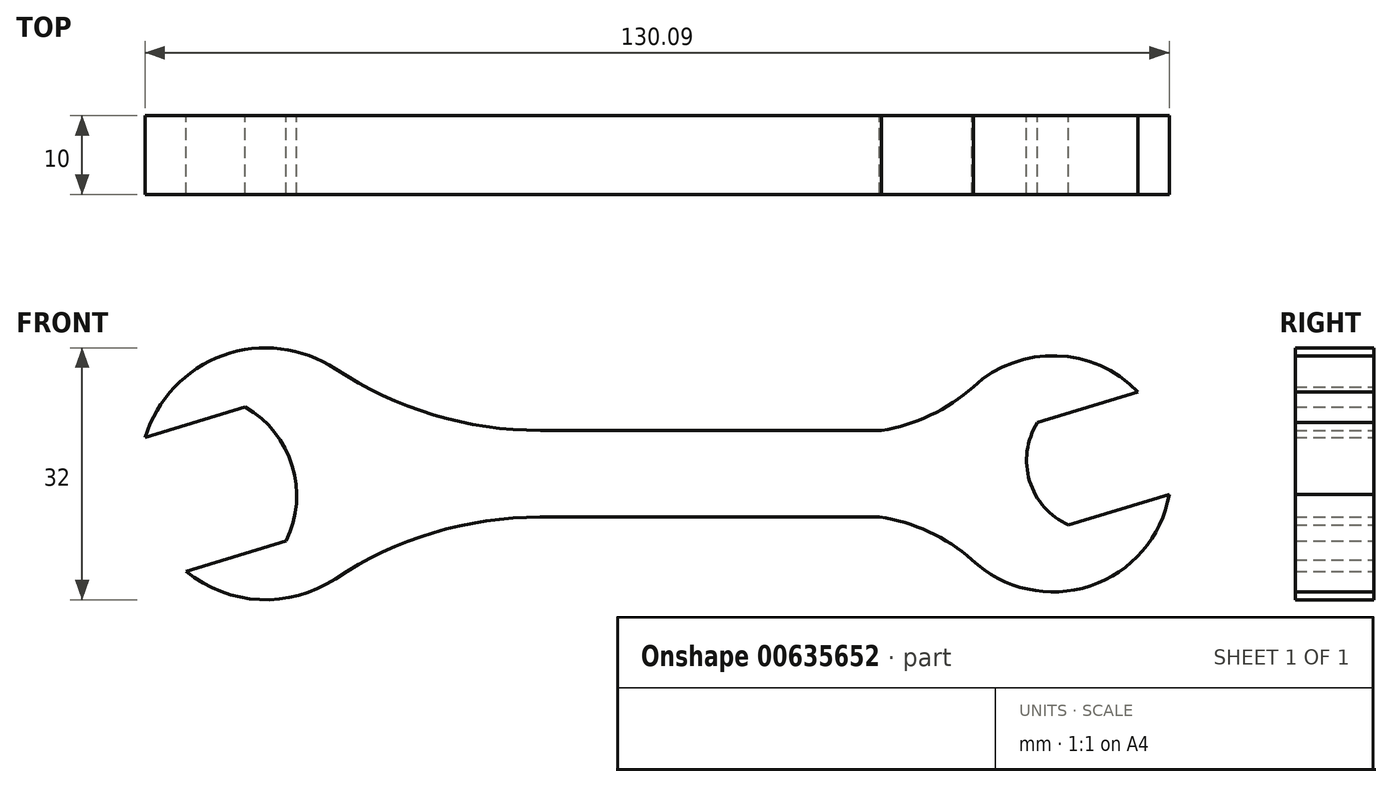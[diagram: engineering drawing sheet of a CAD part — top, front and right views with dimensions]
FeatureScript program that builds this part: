
annotation { "Feature Type Name" : "Feature", "Feature Type Description" : "" }
export const myFeature = defineFeature(function(context is Context, id is Id, definition is map)
    precondition{}
    {
        {
            var Q0;
            Q0=qCreatedBy(makeId("Front.planeOp"),FACE);
            var sketch = newSketch(context, id + "F0", { "sketchPlane" : qUnion([Q0])});
            skLineSegment(sketch, "E0", {"start": v(0, 0) * mm, "end": v(-46.37, 0) * mm, "construction": true});
            skArc(sketch, "E1", {"start": v(-60.12, -12.39) * mm, "mid": v(-34.7, 4.68) * mm, "end": v(-65.32, 4.61) * mm});
            skArc(sketch, "E2", {"start": v(60.8, 10.4) * mm, "mid": v(35.66, -4.39) * mm, "end": v(64.77, -2.6) * mm});
            skLineSegment(sketch, "E3", {"start": v(0, 0) * mm, "end": v(0, 5.08) * mm});
            skLineSegment(sketch, "E4", {"start": v(0, 0) * mm, "end": v(0, -5.48) * mm});
            skArc(sketch, "E5", {"start": v(-41.16, 13.33) * mm, "mid": v(-28.71, 7.5) * mm, "end": v(-15.12, 5.52) * mm});
            skLineSegment(sketch, "E6", {"start": v(-15.12, 5.52) * mm, "end": v(28.2, 5.52) * mm});
            skArc(sketch, "E7", {"start": v(28.2, 5.52) * mm, "mid": v(34.54, 7.5) * mm, "end": v(40.05, 11.22) * mm});
            skArc(sketch, "E8", {"start": v(39.7, -10.91) * mm, "mid": v(34.22, -7.35) * mm, "end": v(27.96, -5.48) * mm});
            skArc(sketch, "E9", {"start": v(-15.15, -5.48) * mm, "mid": v(-28.73, -7.49) * mm, "end": v(-41.16, -13.33) * mm});
            skLineSegment(sketch, "E10", {"start": v(-15.15, -5.48) * mm, "end": v(27.96, -5.48) * mm});
            skLineSegment(sketch, "E11", {"start": v(39.2, -10.4) * mm, "end": v(64.77, -2.6) * mm});
            skLineSegment(sketch, "E12", {"start": v(35.23, 2.6) * mm, "end": v(60.8, 10.4) * mm});
            skLineSegment(sketch, "E13", {"start": v(50, -5.29) * mm, "end": v(50, -7.1) * mm});
            skArc(sketch, "E14", {"start": v(48.01, 6.5) * mm, "mid": v(47.03, -0.9) * mm, "end": v(51.99, -6.5) * mm});
            skLineSegment(sketch, "E15", {"start": v(-46.37, 0) * mm, "end": v(-34, 0) * mm});
            skLineSegment(sketch, "E16", {"start": v(-34, 0) * mm, "end": v(-46.37, 0) * mm});
            skLineSegment(sketch, "E17", {"start": v(-65.32, 4.61) * mm, "end": v(-39.88, 12.39) * mm});
            skLineSegment(sketch, "E18", {"start": v(-60.12, -12.39) * mm, "end": v(-34.68, -4.61) * mm});
            skArc(sketch, "E19", {"start": v(-47.4, -8.5) * mm, "mid": v(-46.64, 1.03) * mm, "end": v(-52.6, 8.5) * mm});
            skSolve(sketch);
        }
        {
            var Q0;
            Q0 = qSketchRegion(id + "F0", true);
            extrude(context, id + "F1", {"entities" : qUnion([Q0]), "depth" : 10 * mm, "offsetDistance" : 25 * mm});
        }
    });
